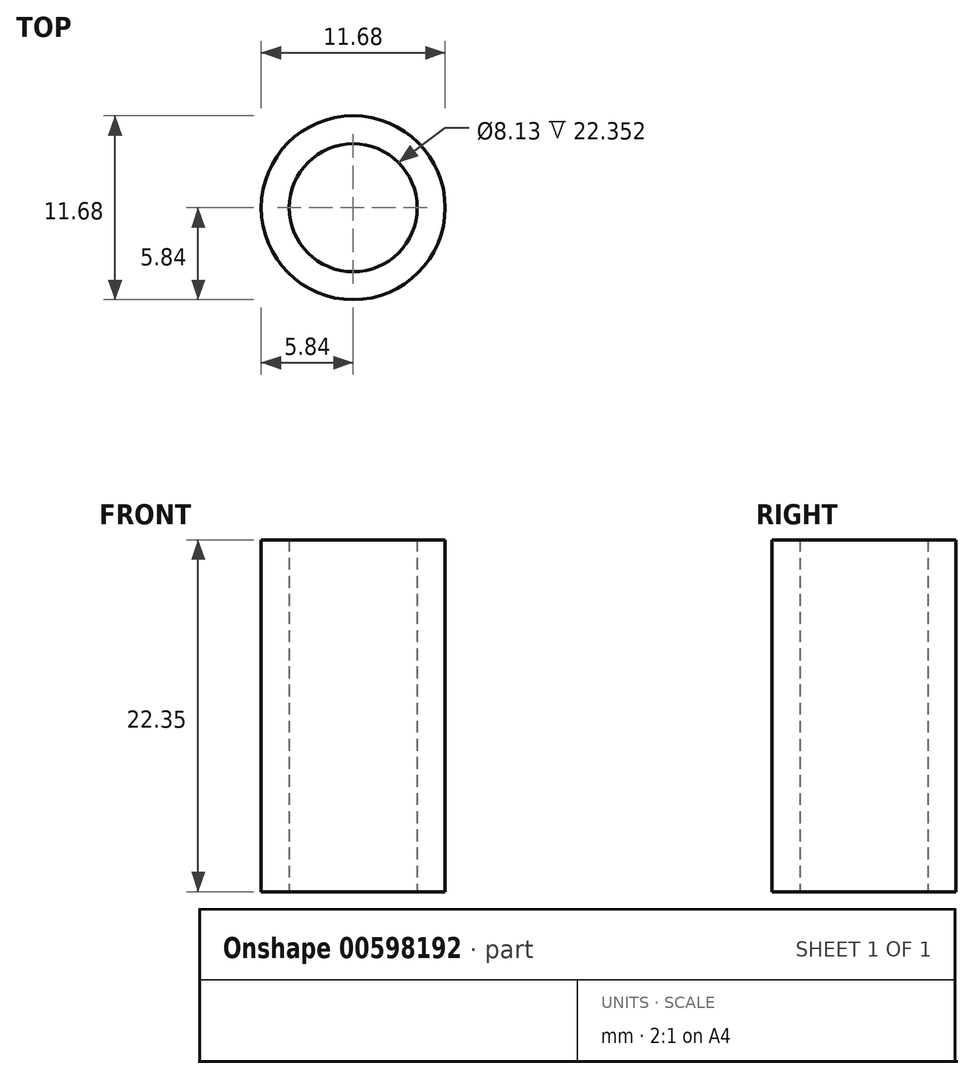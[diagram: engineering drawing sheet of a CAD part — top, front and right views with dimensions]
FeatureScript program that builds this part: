
annotation { "Feature Type Name" : "Feature", "Feature Type Description" : "" }
export const myFeature = defineFeature(function(context is Context, id is Id, definition is map)
    precondition{}
    {
        {
            var Q0;
            Q0=qCreatedBy(makeId("Top.planeOp"),FACE);
            var sketch = newSketch(context, id + "F0", { "sketchPlane" : qUnion([Q0])});
            skCircle(sketch, "E0", {"center": v(0, 0) * mm, "radius": 5.84 * mm});
            skCircle(sketch, "E1", {"center": v(0, 0) * mm, "radius": 4.06 * mm});
            skSolve(sketch);
        }
        {
            var Q0;
            Q0 = qSketchRegion(id + "F0", true);
            extrude(context, id + "F1", {"entities" : qUnion([Q0]), "depth" : 22.35 * mm, "offsetDistance" : 25.4 * mm});
        }
    });
